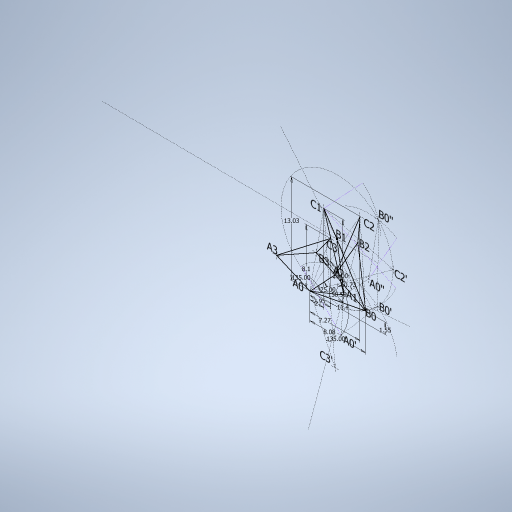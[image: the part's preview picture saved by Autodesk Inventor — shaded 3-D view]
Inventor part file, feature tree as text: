
AUTODESK INVENTOR PART (.ipt)
format: ipt  version: 2024 (Build 280153000, 153)  size: 284,160 bytes
history: native  units: in
note: dims shown in document units (in); Inventor stores cm internally (conversion verified against a paired STEP export)
features: sketch x1
ambient origin geometry x8: Origin, YZ Plane, XZ Plane, XY Plane, X Axis, Y Axis, Z Axis, Center Point
feature tree (1):
  sketch  "Sketch1"  dims[d0=0.4488in d1=0.0787in d2=0.2862in d3=0.513in d4=0.1161in d5=0.3189in d6=0.3181in d7=0.061in d8=0.1718in d9=135.0deg d10=0.1718in d11=135.0deg d12=1.0898in d13=0.4173in]
